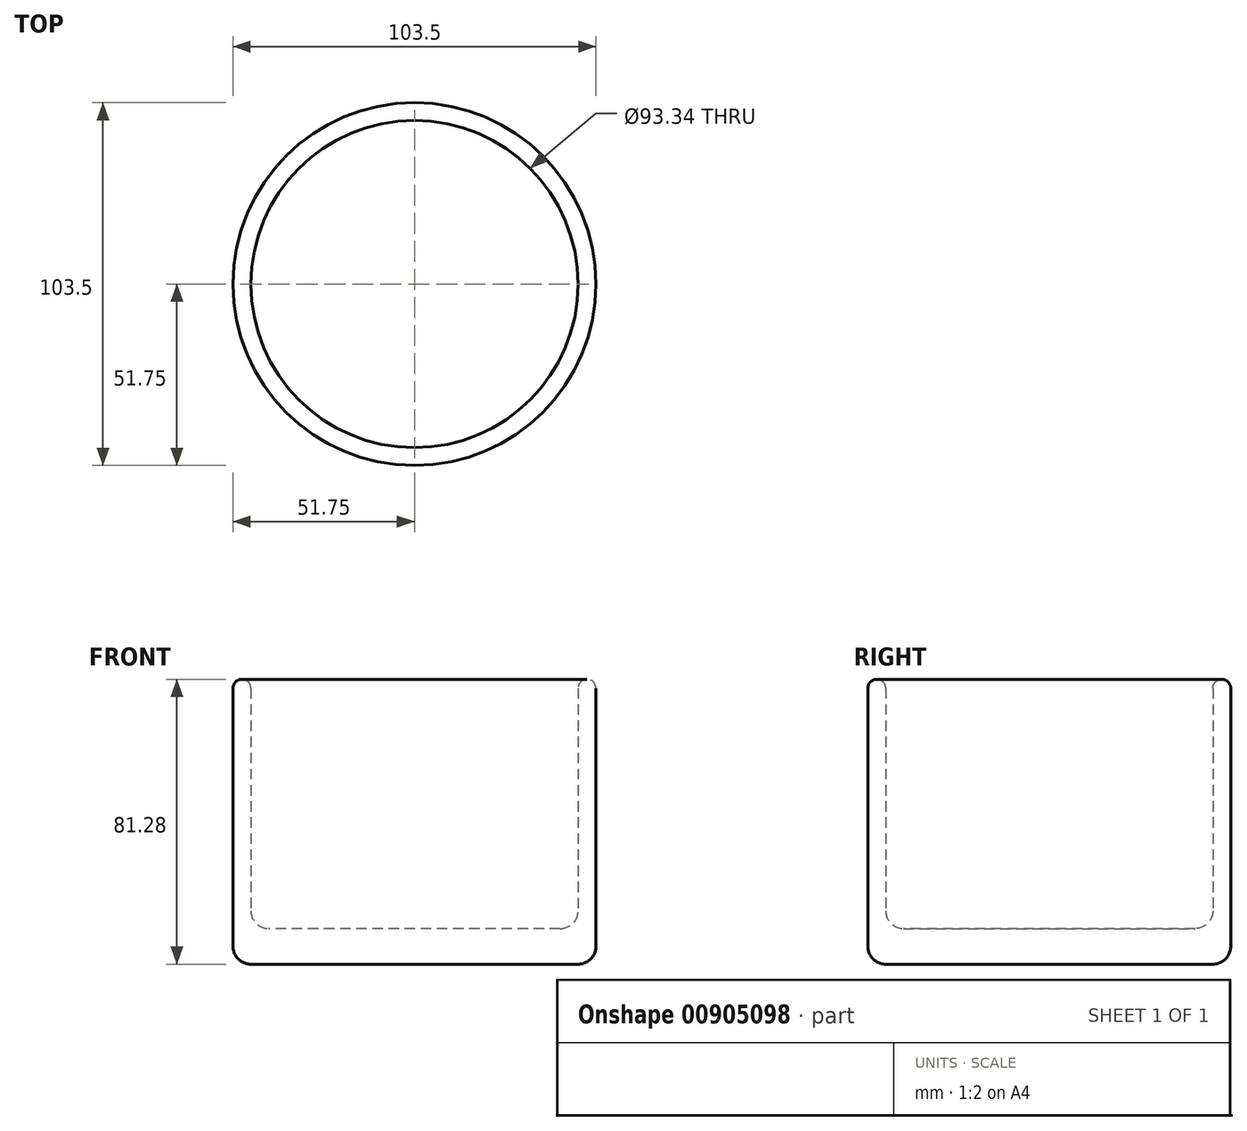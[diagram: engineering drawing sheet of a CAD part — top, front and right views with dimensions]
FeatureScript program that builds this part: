
annotation { "Feature Type Name" : "Feature", "Feature Type Description" : "" }
export const myFeature = defineFeature(function(context is Context, id is Id, definition is map)
    precondition{}
    {
        {
            var Q0;
            Q0=qCreatedBy(makeId("Top.planeOp"),FACE);
            var sketch = newSketch(context, id + "F0", { "sketchPlane" : qUnion([Q0])});
            skCircle(sketch, "E0", {"center": v(0, 0) * mm, "radius": 51.75 * mm});
            skSolve(sketch);
        }
        {
            var Q0;
            Q0=makeQuery(id+"F0.imprint","IMPRINT",FACE,{"disambiguationData":[TD([[makeQuery(id+"F0.imprint","IMPRINT",EDGE,{"derivedFrom":sQuery(id+"F0.wireOp",EDGE,"E0")}),1.0]])]});
            extrude(context, id + "F1", {"entities" : qUnion([Q0]), "depth" : 76.2 * mm, "offsetDistance" : 25.4 * mm});
        }
        {
            var Q0;
            Q0=makeQuery(id+"F1.opExtrude","CAP_FACE",FACE,{"disambiguationData":[OSD([sQuery(id+"F0.wireOp",EDGE,"E0")])],"isStart":false});
            shell(context, id + "F2", {"entities" : qUnion([Q0]), "thickness" : 5.08 * mm});
        }
        {
            var Q0;
            Q0 = qSketchRegion(id + "F0", true);
            var Q1;
            Q1=makeQuery(id+"F1.opExtrude","CAP_FACE",FACE,{"disambiguationData":[OSD([sQuery(id+"F0.wireOp",EDGE,"E0")])],"isStart":true});
            extrude(context, id + "F3", {"entities" : qUnion([Q0, Q1]), "operationType" : NewBodyOperationType.ADD, "depth" : -5.08 * mm, "offsetDistance" : 25.4 * mm});
        }
        {
            var Q0;
            Q0=makeQuery(id+"F1.opExtrude","CAP_FACE",FACE,{"disambiguationData":[OSD([sQuery(id+"F0.wireOp",EDGE,"E0")])],"isStart":false});
            fillet(context, id + "F4", {"entities" : qUnion([Q0]), "radius" : 2.54 * mm, "tangentPropagation" : true, "allowEdgeOverflow" : false});
        }
        {
            var Q0;
            {var subQ0=sQuery(id+"F0.wireOp",EDGE,"E0");Q0=makeQuery(id+"F2.opShell","OFFSET_EDGE",EDGE,{"disambiguationData":[OSD([subQ0]),TDD([makeQuery(id+"F1.opExtrude","CAP_EDGE",EDGE,{"disambiguationData":[OSD([subQ0])],"isStart":true})])]});}
            fillet(context, id + "F5", {"entities" : qUnion([Q0]), "radius" : 5.08 * mm, "tangentPropagation" : true, "allowEdgeOverflow" : false});
        }
        {
            var Q0;
            {var subQ0=sQuery(id+"F0.wireOp",EDGE,"E0");Q0=makeQuery(id+"F3.opExtrude","CAP_EDGE",EDGE,{"disambiguationData":[OSD([subQ0]),TDD([makeQuery(id+"F0.imprint","IMPRINT",EDGE,{"derivedFrom":subQ0})])],"isStart":false});}
            fillet(context, id + "F6", {"entities" : qUnion([Q0]), "radius" : 5.08 * mm, "tangentPropagation" : true, "allowEdgeOverflow" : false});
        }
    });
